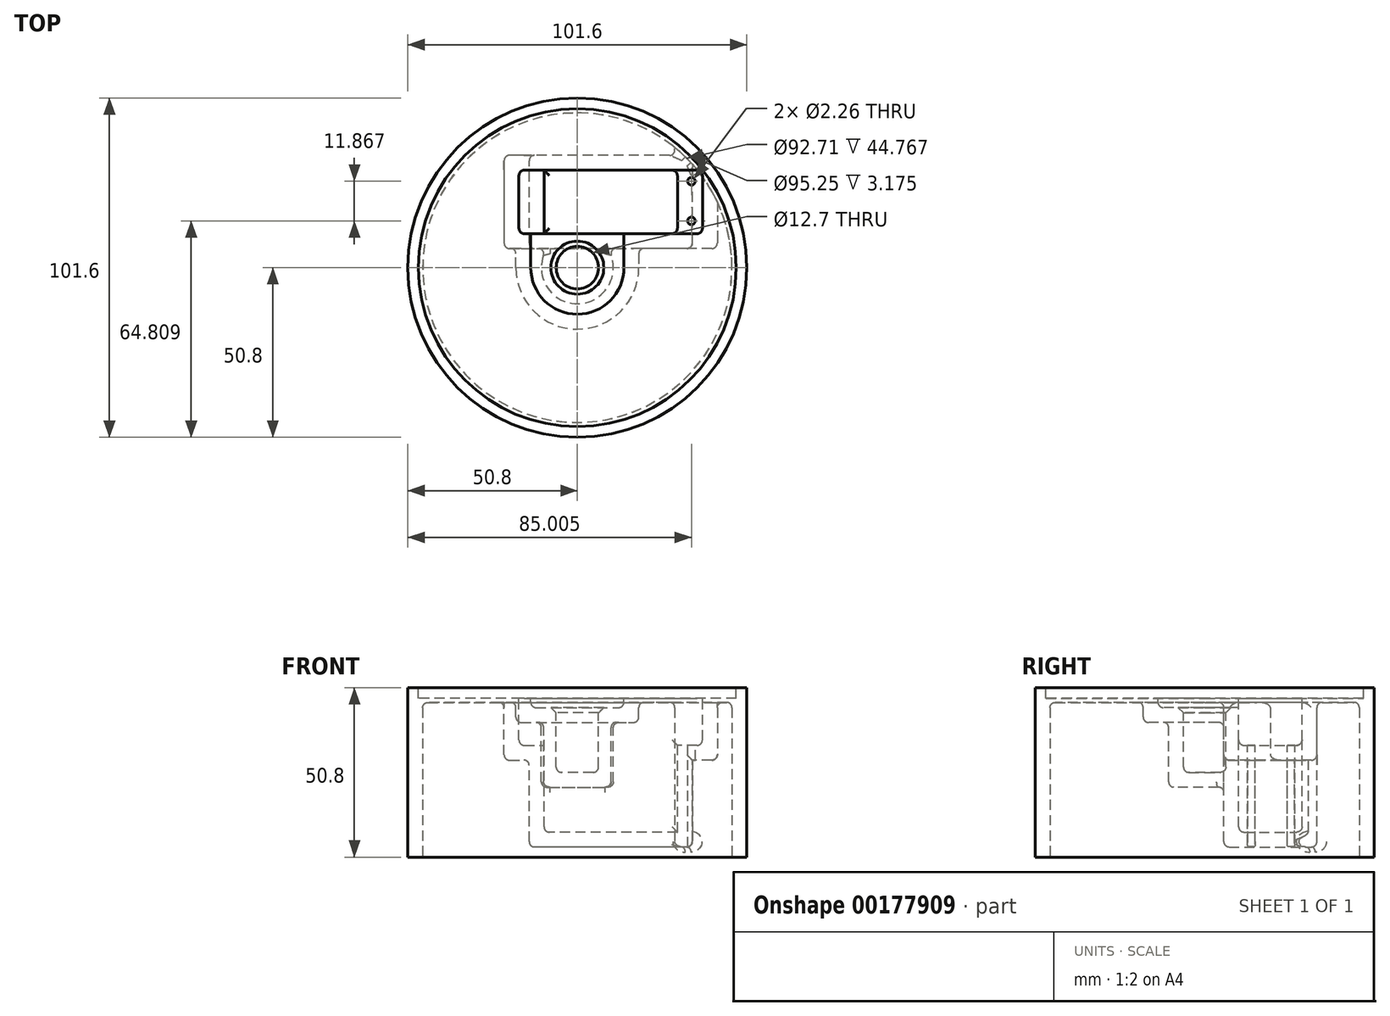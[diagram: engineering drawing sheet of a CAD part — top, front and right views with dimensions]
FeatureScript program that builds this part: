
annotation { "Feature Type Name" : "Feature", "Feature Type Description" : "" }
export const myFeature = defineFeature(function(context is Context, id is Id, definition is map)
    precondition{}
    {
        {
            var Q0;
            Q0=qCreatedBy(makeId("Top.planeOp"),FACE);
            var sketch = newSketch(context, id + "F0", { "sketchPlane" : qUnion([Q0])});
            skCircle(sketch, "E0", {"center": v(0, 0) * mm, "radius": 50.8 * mm});
            skSolve(sketch);
        }
        {
            var Q0;
            Q0=qSketchRegion(id+"F0",true);
            extrude(context, id + "F1", {"entities" : qUnion([Q0]), "depth" : 50.8 * mm});
        }
        {
            var Q0;
            Q0=makeQuery(id+"F1.opExtrude","CAP_FACE",FACE,{"disambiguationData":[OSD([sQuery(id+"F0.wireOp",EDGE,"E0")])],"isStart":false});
            var sketch = newSketch(context, id + "F2", { "sketchPlane" : qUnion([Q0])});
            skCircle(sketch, "E1", {"center": v(0, 0) * mm, "radius": 13.02 * mm});
            skCircle(sketch, "E2", {"center": v(0, 19.69) * mm, "radius": 6.67 * mm});
            skSolve(sketch);
        }
        {
            var Q0;
            Q0=makeQuery(id+"F2.imprint","IMPRINT",FACE,{"disambiguationData":[TD([[makeQuery(id+"F2.imprint","IMPRINT",EDGE,{"derivedFrom":sQuery(id+"F2.wireOp",EDGE,"E1")}),-1.0]])]});
            var sketch = newSketch(context, id + "F3", { "sketchPlane" : qUnion([Q0])});
            skLineSegment(sketch, "E3.bottom", {"start": v(30, 10.19) * mm, "end": v(-10, 10.18) * mm});
            skLineSegment(sketch, "E3.top", {"start": v(30, 29.19) * mm, "end": v(-10, 29.18) * mm});
            skLineSegment(sketch, "E3.left", {"start": v(30, 10.19) * mm, "end": v(30, 29.19) * mm});
            skLineSegment(sketch, "E3.right", {"start": v(-10, 10.18) * mm, "end": v(-10, 29.18) * mm});
            skPoint(sketch, "E3.middle", {"position": v(10, 19.69) * mm});
            skSolve(sketch);
        }
        {
            var Q0;
            Q0=qSketchRegion(id+"F3",true);
            extrude(context, id + "F4", {"entities" : qUnion([Q0]), "operationType" : NewBodyOperationType.REMOVE, "oppositeDirection" : true, "depth" : 43.3 * mm});
        }
        {
            var Q0;
            Q0=makeQuery(id+"F2.imprint","IMPRINT",FACE,{"disambiguationData":[TD([[makeQuery(id+"F2.imprint","IMPRINT",EDGE,{"derivedFrom":sQuery(id+"F2.wireOp",EDGE,"E1")}),-1.0]])]});
            var sketch = newSketch(context, id + "F5", { "sketchPlane" : qUnion([Q0])});
            skLineSegment(sketch, "E4.0", {"start": v(-10, 10.18) * mm, "end": v(-10, 29.18) * mm});
            skLineSegment(sketch, "E4.1", {"start": v(30, 10.19) * mm, "end": v(30, 29.19) * mm});
            skLineSegment(sketch, "E5", {"start": v(-10, 29.18) * mm, "end": v(-17.5, 29.18) * mm});
            skLineSegment(sketch, "E6", {"start": v(-17.5, 29.18) * mm, "end": v(-17.5, 10.18) * mm});
            skLineSegment(sketch, "E7", {"start": v(-17.5, 10.18) * mm, "end": v(-10, 10.18) * mm});
            skLineSegment(sketch, "E8", {"start": v(30, 29.18) * mm, "end": v(37.5, 29.18) * mm});
            skLineSegment(sketch, "E9", {"start": v(37.5, 29.19) * mm, "end": v(37.5, 10.18) * mm});
            skLineSegment(sketch, "E10", {"start": v(37.5, 10.18) * mm, "end": v(30, 10.18) * mm});
            skSolve(sketch);
        }
        {
            var Q0;
            Q0=qSketchRegion(id+"F5",true);
            extrude(context, id + "F6", {"entities" : qUnion([Q0]), "operationType" : NewBodyOperationType.REMOVE, "oppositeDirection" : true, "depth" : (43.3 - 26) * mm});
        }
        {
            var Q0;
            Q0=makeQuery(id+"F2.imprint","IMPRINT",FACE,{"disambiguationData":[TD([[makeQuery(id+"F2.imprint","IMPRINT",EDGE,{"derivedFrom":sQuery(id+"F2.wireOp",EDGE,"E1")}),-1.0]])]});
            var sketch = newSketch(context, id + "F7", { "sketchPlane" : qUnion([Q0])});
            skArc(sketch, "E11", {"start": v(-13.97, 0) * mm, "mid": v(0, -13.97) * mm, "end": v(13.97, 0) * mm});
            skLineSegment(sketch, "E12", {"start": v(-13.97, 0) * mm, "end": v(-13.97, 10.18) * mm});
            skLineSegment(sketch, "E13", {"start": v(-13.97, 10.18) * mm, "end": v(13.97, 10.18) * mm});
            skLineSegment(sketch, "E14", {"start": v(13.97, 10.18) * mm, "end": v(13.97, 0) * mm});
            skSolve(sketch);
        }
        {
            var Q0;
            Q0=qSketchRegion(id+"F7",true);
            var Q1;
            Q1=makeQuery(id+"F6.boolean.opBoolean","COPY",FACE,{"derivedFrom":makeQuery(id+"F6.opExtrude","CAP_FACE",FACE,{"disambiguationData":[OSD([sQuery(id+"F5.wireOp",EDGE,"E4.0"),sQuery(id+"F5.wireOp",EDGE,"E5"),sQuery(id+"F5.wireOp",EDGE,"E6"),sQuery(id+"F5.wireOp",EDGE,"E7")])],"isStart":false})});
            extrude(context, id + "F8", {"entities" : qUnion([Q0]), "operationType" : NewBodyOperationType.REMOVE, "oppositeDirection" : true, "endBoundEntityFace" : qUnion([Q1]), "depth" : 6 * mm});
        }
        {
            var Q0;
            Q0=makeQuery(id+"F2.imprint","IMPRINT",FACE,{"disambiguationData":[TD([[makeQuery(id+"F2.imprint","IMPRINT",EDGE,{"derivedFrom":sQuery(id+"F2.wireOp",EDGE,"E1")}),1.0]])]});
            var sketch = newSketch(context, id + "F9", { "sketchPlane" : qUnion([Q0])});
            skCircle(sketch, "E15", {"center": v(0, 0) * mm, "radius": 6.35 * mm});
            skSolve(sketch);
        }
        {
            var Q0;
            Q0=qSketchRegion(id+"F9",true);
            extrude(context, id + "F10", {"entities" : qUnion([Q0]), "operationType" : NewBodyOperationType.REMOVE, "oppositeDirection" : true, "depth" : 25.4 * mm});
        }
        {
            var Q0;
            Q0=makeQuery(id+"F1.opExtrude","CAP_FACE",FACE,{"disambiguationData":[OSD([sQuery(id+"F0.wireOp",EDGE,"E0")])],"isStart":true});
            shell(context, id + "F11", {"entities" : qUnion([Q0]), "thickness" : 4.44 * mm});
        }
        {
            var Q0;
            Q0=makeQuery(id+"F2.imprint","IMPRINT",FACE,{"disambiguationData":[TD([[makeQuery(id+"F2.imprint","IMPRINT",EDGE,{"derivedFrom":sQuery(id+"F2.wireOp",EDGE,"E1")}),-1.0]])]});
            var sketch = newSketch(context, id + "F12", { "sketchPlane" : qUnion([Q0])});
            skCircle(sketch, "E16", {"center": v(0, 0) * mm, "radius": 47.62 * mm});
            skSolve(sketch);
        }
        {
            var Q0;
            Q0=qSketchRegion(id+"F12",true);
            extrude(context, id + "F13", {"entities" : qUnion([Q0]), "operationType" : NewBodyOperationType.REMOVE, "oppositeDirection" : true, "depth" : 3.17 * mm});
        }
        {
            var Q0;
            Q0=makeQuery(id+"F8.boolean.opBoolean","COPY",EDGE,{"derivedFrom":makeQuery(id+"F8.opExtrude","CAP_EDGE",EDGE,{"disambiguationData":[OSD([sQuery(id+"F7.wireOp",EDGE,"E12")])],"isStart":false})});
            var Q1;
            Q1=makeQuery(id+"F6.boolean.opBoolean","COPY",EDGE,{"derivedFrom":makeQuery(id+"F6.opExtrude","CAP_EDGE",EDGE,{"disambiguationData":[OSD([sQuery(id+"F5.wireOp",EDGE,"E6")])],"isStart":false})});
            var Q2;
            Q2=makeQuery(id+"F6.boolean.opBoolean","COPY",EDGE,{"derivedFrom":makeQuery(id+"F6.opExtrude","CAP_EDGE",EDGE,{"disambiguationData":[OSD([sQuery(id+"F5.wireOp",EDGE,"E5")])],"isStart":false})});
            var Q3;
            Q3=makeQuery(id+"F6.boolean.opBoolean","COPY",EDGE,{"derivedFrom":makeQuery(id+"F6.opExtrude","CAP_EDGE",EDGE,{"disambiguationData":[OSD([sQuery(id+"F5.wireOp",EDGE,"E4.0")])],"isStart":false})});
            var Q4;
            Q4=makeQuery(id+"F4.boolean.opBoolean","COPY",EDGE,{"derivedFrom":makeQuery(id+"F4.opExtrude","CAP_EDGE",EDGE,{"disambiguationData":[OSD([sQuery(id+"F3.wireOp",EDGE,"E3.right")])],"isStart":false})});
            var Q5;
            Q5=makeQuery(id+"F4.boolean.opBoolean","COPY",EDGE,{"derivedFrom":makeQuery(id+"F4.opExtrude","CAP_EDGE",EDGE,{"disambiguationData":[OSD([sQuery(id+"F3.wireOp",EDGE,"E3.top")])],"isStart":false})});
            var Q6;
            Q6=makeQuery(id+"F6.boolean.opBoolean","COPY",EDGE,{"derivedFrom":makeQuery(id+"F6.opExtrude","SWEPT_EDGE",EDGE,{"disambiguationData":[OSD([sQuery(id+"F5.wireOp",EDGE,"E6"),sQuery(id+"F5.wireOp",EDGE,"E7")])]})});
            var Q7;
            Q7=makeQuery(id+"F6.boolean.opBoolean","COPY",EDGE,{"derivedFrom":makeQuery(id+"F6.opExtrude","CAP_EDGE",EDGE,{"disambiguationData":[OSD([sQuery(id+"F5.wireOp",EDGE,"E7")])],"isStart":false})});
            var Q8;
            Q8=makeQuery(id+"F4.boolean.opBoolean","COPY",EDGE,{"derivedFrom":makeQuery(id+"F4.opExtrude","CAP_EDGE",EDGE,{"disambiguationData":[OSD([sQuery(id+"F3.wireOp",EDGE,"E3.bottom")])],"isStart":false})});
            var Q9;
            Q9=makeQuery(id+"F4.boolean.opBoolean","COPY",EDGE,{"derivedFrom":makeQuery(id+"F4.opExtrude","SWEPT_EDGE",EDGE,{"disambiguationData":[OSD([sQuery(id+"F3.wireOp",EDGE,"E3.bottom"),sQuery(id+"F3.wireOp",EDGE,"E3.left")])]})});
            var Q10;
            Q10=makeQuery(id+"F4.boolean.opBoolean","COPY",EDGE,{"derivedFrom":makeQuery(id+"F4.opExtrude","SWEPT_EDGE",EDGE,{"disambiguationData":[OSD([sQuery(id+"F3.wireOp",EDGE,"E3.top"),sQuery(id+"F3.wireOp",EDGE,"E3.left")])]})});
            var Q11;
            Q11=makeQuery(id+"F6.boolean.opBoolean","COPY",EDGE,{"derivedFrom":makeQuery(id+"F6.opExtrude","CAP_EDGE",EDGE,{"disambiguationData":[OSD([sQuery(id+"F5.wireOp",EDGE,"E8")])],"isStart":false})});
            var Q12;
            Q12=makeQuery(id+"F6.boolean.opBoolean","COPY",EDGE,{"derivedFrom":makeQuery(id+"F6.opExtrude","SWEPT_EDGE",EDGE,{"disambiguationData":[OSD([sQuery(id+"F5.wireOp",EDGE,"E8"),sQuery(id+"F5.wireOp",EDGE,"E9")])]})});
            var Q13;
            Q13=makeQuery(id+"F6.boolean.opBoolean","COPY",EDGE,{"derivedFrom":makeQuery(id+"F6.opExtrude","SWEPT_EDGE",EDGE,{"disambiguationData":[OSD([sQuery(id+"F5.wireOp",EDGE,"E9"),sQuery(id+"F5.wireOp",EDGE,"E10")])]})});
            var Q14;
            Q14=makeQuery(id+"F6.boolean.opBoolean","COPY",EDGE,{"derivedFrom":makeQuery(id+"F6.opExtrude","CAP_EDGE",EDGE,{"disambiguationData":[OSD([sQuery(id+"F5.wireOp",EDGE,"E9")])],"isStart":false})});
            var Q15;
            Q15=makeQuery(id+"F6.boolean.opBoolean","COPY",EDGE,{"derivedFrom":makeQuery(id+"F6.opExtrude","CAP_EDGE",EDGE,{"disambiguationData":[OSD([sQuery(id+"F5.wireOp",EDGE,"E10")])],"isStart":false})});
            var Q16;
            Q16=makeQuery(id+"F6.boolean.opBoolean","COPY",EDGE,{"derivedFrom":makeQuery(id+"F6.opExtrude","CAP_EDGE",EDGE,{"disambiguationData":[OSD([sQuery(id+"F5.wireOp",EDGE,"E4.1")])],"isStart":false})});
            var Q17;
            Q17=makeQuery(id+"F8.boolean.opBoolean","COPY",EDGE,{"derivedFrom":makeQuery(id+"F8.opExtrude","SWEPT_EDGE",EDGE,{"disambiguationData":[OSD([sQuery(id+"F7.wireOp",EDGE,"E12"),sQuery(id+"F7.wireOp",EDGE,"E13")])]})});
            var Q18;
            {var subQ0=sQuery(id+"F0.wireOp",EDGE,"E0");Q18=makeQuery(id+"F11.opShell","OFFSET_EDGE",EDGE,{"disambiguationData":[OSD([subQ0]),TDD([makeQuery(id+"F1.opExtrude","CAP_EDGE",EDGE,{"disambiguationData":[OSD([subQ0])],"isStart":false})])]});}
            var Q19;
            Q19=makeQuery(id+"F6.boolean.opBoolean","COPY",EDGE,{"derivedFrom":makeQuery(id+"F6.opExtrude","SWEPT_EDGE",EDGE,{"disambiguationData":[OSD([sQuery(id+"F5.wireOp",EDGE,"E5"),sQuery(id+"F5.wireOp",EDGE,"E6")])]})});
            var Q20;
            Q20=makeQuery(id+"F11.opShell","OFFSET_FACE",FACE,{"disambiguationData":[OSD([sQuery(id+"F3.wireOp",EDGE,"E3.bottom"),sQuery(id+"F3.wireOp",EDGE,"E3.top"),sQuery(id+"F3.wireOp",EDGE,"E3.left"),sQuery(id+"F3.wireOp",EDGE,"E3.right")])]});
            var Q21;
            Q21=makeQuery(id+"F11.opShell","OFFSET_FACE",FACE,{"disambiguationData":[OSD([sQuery(id+"F3.wireOp",EDGE,"E3.bottom"),sQuery(id+"F5.wireOp",EDGE,"E7"),sQuery(id+"F5.wireOp",EDGE,"E10")])]});
            var Q22;
            Q22=makeQuery(id+"F11.opShell","OFFSET_FACE",FACE,{"disambiguationData":[OSD([sQuery(id+"F3.wireOp",EDGE,"E3.right")])]});
            var Q23;
            Q23=makeQuery(id+"F11.opShell","OFFSET_FACE",FACE,{"disambiguationData":[OSD([sQuery(id+"F3.wireOp",EDGE,"E3.top"),sQuery(id+"F5.wireOp",EDGE,"E5"),sQuery(id+"F5.wireOp",EDGE,"E8")])]});
            var Q24;
            {var subQ0=sQuery(id+"F5.wireOp",EDGE,"E6");Q24=makeQuery(id+"F11.opShell","OFFSET_EDGE",EDGE,{"disambiguationData":[OSD([subQ0]),TDD([makeQuery(id+"F6.boolean.opBoolean","COPY",EDGE,{"derivedFrom":makeQuery(id+"F6.opExtrude","CAP_EDGE",EDGE,{"disambiguationData":[OSD([subQ0])],"isStart":false})})])]});}
            var Q25;
            {var subQ0=sQuery(id+"F9.wireOp",EDGE,"E15");Q25=makeQuery(id+"F11.opShell","OFFSET_FACE",FACE,{"disambiguationData":[OSD([subQ0]),TDD([makeQuery(id+"F10.boolean.opBoolean","COPY",FACE,{"derivedFrom":makeQuery(id+"F10.opExtrude","SWEPT_FACE",FACE,{"disambiguationData":[OSD([subQ0])]})})])]});}
            var Q26;
            Q26=makeQuery(id+"F11.opShell","OFFSET_FACE",FACE,{"disambiguationData":[OSD([sQuery(id+"F7.wireOp",EDGE,"E11")])]});
            var Q27;
            {var subQ0=sQuery(id+"F5.wireOp",EDGE,"E9");Q27=makeQuery(id+"F11.opShell","OFFSET_EDGE",EDGE,{"disambiguationData":[OSD([subQ0]),TDD([makeQuery(id+"F6.boolean.opBoolean","COPY",EDGE,{"derivedFrom":makeQuery(id+"F6.opExtrude","CAP_EDGE",EDGE,{"disambiguationData":[OSD([subQ0])],"isStart":false})})])]});}
            var Q28;
            Q28=makeQuery(id+"F10.boolean.opBoolean","COPY",EDGE,{"derivedFrom":makeQuery(id+"F10.opExtrude","CAP_EDGE",EDGE,{"disambiguationData":[OSD([sQuery(id+"F9.wireOp",EDGE,"E15")])],"isStart":false})});
            fillet(context, id + "F14", {"entities" : qUnion([Q0, Q1, Q2, Q3, Q4, Q5, Q6, Q7, Q8, Q9, Q10, Q11, Q12, Q13, Q14, Q15, Q16, Q17, Q18, Q19, Q20, Q21, Q22, Q23, Q24, Q25, Q26, Q27, Q28]), "radius" : 1.59 * mm, "tangentPropagation" : true, "allowEdgeOverflow" : false});
        }
        {
            var Q0;
            Q0=makeQuery(id+"F10.boolean.opBoolean","INTERSECT",EDGE,{"derivedFrom":[makeQuery(id+"F8.boolean.opBoolean","COPY",FACE,{"derivedFrom":makeQuery(id+"F8.opExtrude","CAP_FACE",FACE,{"disambiguationData":[OSD([sQuery(id+"F7.wireOp",EDGE,"E11"),sQuery(id+"F7.wireOp",EDGE,"E12"),sQuery(id+"F7.wireOp",EDGE,"E13"),sQuery(id+"F7.wireOp",EDGE,"E14")])],"isStart":false})}),makeQuery(id+"F10.opExtrude","SWEPT_FACE",FACE,{"disambiguationData":[OSD([sQuery(id+"F9.wireOp",EDGE,"E15")])]})]});
            chamfer(context, id + "F15", {"entities" : qUnion([Q0]), "width" : 1.59 * mm, "tangentPropagation" : true});
        }
        {
            var Q0;
            Q0=makeQuery(id+"F6.boolean.opBoolean","COPY",FACE,{"derivedFrom":makeQuery(id+"F6.opExtrude","CAP_FACE",FACE,{"disambiguationData":[OSD([sQuery(id+"F5.wireOp",EDGE,"E4.1"),sQuery(id+"F5.wireOp",EDGE,"E8"),sQuery(id+"F5.wireOp",EDGE,"E9"),sQuery(id+"F5.wireOp",EDGE,"E10")])],"isStart":false})});
            var sketch = newSketch(context, id + "F16", { "sketchPlane" : qUnion([Q0])});
            skLineSegment(sketch, "E17", {"start": v(34.2, 25.88) * mm, "end": v(34.2, 14) * mm});
            skSolve(sketch);
        }
        {
            var Q0;
            Q0=sQuery(id+"F16.wireOp",VERTEX,"E17.start");
            var Q1;
            Q1=sQuery(id+"F16.wireOp",VERTEX,"E17.end");
            var Q2;
            Q2=makeQuery(id+"F1.opExtrude","SWEPT_BODY",BODY,{"disambiguationData":[OSD([sQuery(id+"F0.wireOp",EDGE,"E0")])]});
            hole(context, id + "F17", {"style" : HoleStyle.SIMPLE, "endStyle" : HoleEndStyle.THROUGH, "standardTappedOrClearance" : lookupTablePath({ "standard" : "ANSI", "engagement" : "75%", "pitch" : "40 tpi", "size" : "#4", "type" : "Tapped" }), "standardBlindInLast" : lookupTablePath({ "standard" : "ANSI", "engagement" : "75%", "pitch" : "40 tpi", "size" : "#4", "type" : "Tapped" }), "holeDiameter" : 2.26 * mm, "locations" : qUnion([Q0, Q1]), "scope" : qUnion([Q2]), "isTappedThrough" : true, "majorDiameter" : 2.84 * mm, "showTappedDepth" : true});
        }
    });
